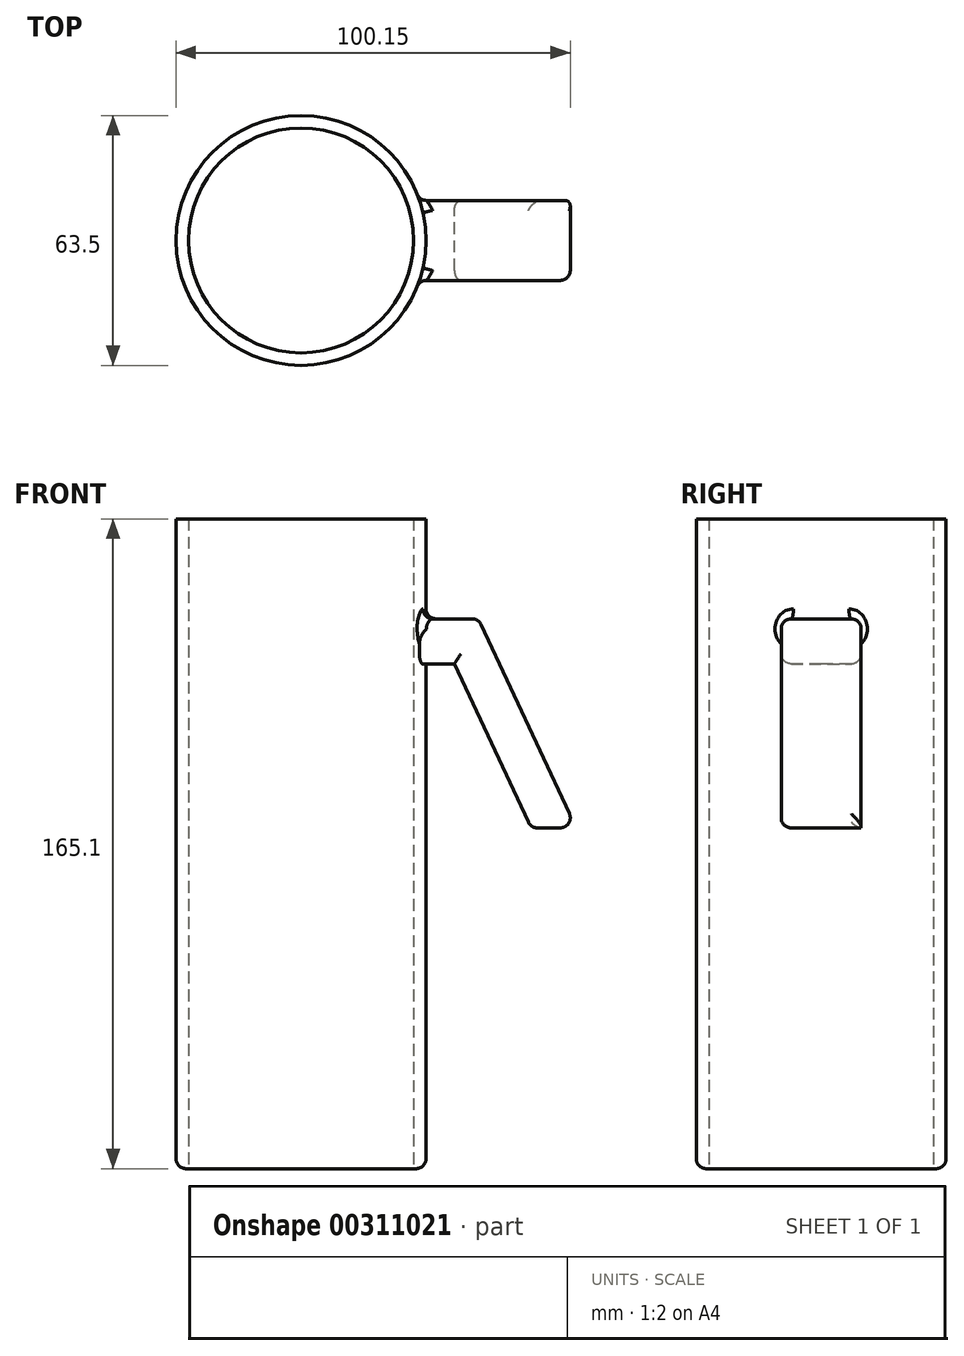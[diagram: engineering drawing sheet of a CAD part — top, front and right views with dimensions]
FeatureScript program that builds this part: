
annotation { "Feature Type Name" : "Feature", "Feature Type Description" : "" }
export const myFeature = defineFeature(function(context is Context, id is Id, definition is map)
    precondition{}
    {
        {
            var Q0;
            Q0=qCreatedBy(makeId("Front.planeOp"),FACE);
            var sketch = newSketch(context, id + "F0", { "sketchPlane" : qUnion([Q0])});
            skLineSegment(sketch, "E0.bottom", {"start": v(31.75, -82.55) * mm, "end": v(-31.75, -82.55) * mm});
            skLineSegment(sketch, "E0.top", {"start": v(31.75, 82.55) * mm, "end": v(-31.75, 82.55) * mm});
            skLineSegment(sketch, "E0.left", {"start": v(31.75, -82.55) * mm, "end": v(31.75, 82.55) * mm});
            skLineSegment(sketch, "E0.right", {"start": v(-31.75, -82.55) * mm, "end": v(-31.75, 82.55) * mm});
            skPoint(sketch, "E0.middle", {"position": v(0, 0) * mm});
            skLineSegment(sketch, "E1", {"start": v(-28.58, 82.55) * mm, "end": v(-28.57, -79.38) * mm});
            skLineSegment(sketch, "E2", {"start": v(-28.57, -79.38) * mm, "end": v(29.2, -79.38) * mm});
            skLineSegment(sketch, "E3", {"start": v(29.2, -79.38) * mm, "end": v(29.21, 82.55) * mm});
            skLineSegment(sketch, "E4", {"start": v(29.21, 57.15) * mm, "end": v(45.09, 57.15) * mm});
            skLineSegment(sketch, "E5", {"start": v(45.09, 57.15) * mm, "end": v(69.85, 4.04) * mm});
            skLineSegment(sketch, "E6", {"start": v(69.85, 4.04) * mm, "end": v(58.42, 4.04) * mm});
            skLineSegment(sketch, "E7", {"start": v(58.42, 4.04) * mm, "end": v(38.98, 45.72) * mm});
            skLineSegment(sketch, "E8", {"start": v(38.98, 45.72) * mm, "end": v(29.21, 45.72) * mm});
            skSolve(sketch);
        }
        {
            var Q0;
            Q0=qCreatedBy(makeId("Top.planeOp"),FACE);
            var sketch = newSketch(context, id + "F1", { "sketchPlane" : qUnion([Q0])});
            skCircle(sketch, "E9", {"center": v(0, 0) * mm, "radius": 28.58 * mm});
            skCircle(sketch, "E10", {"center": v(0, 0) * mm, "radius": 31.75 * mm});
            skSolve(sketch);
        }
        {
            var Q0;
            Q0=makeQuery(id+"F1.imprint","IMPRINT",FACE,{"disambiguationData":[TD([[makeQuery(id+"F1.imprint","IMPRINT",EDGE,{"derivedFrom":sQuery(id+"F1.wireOp",EDGE,"E9")}),-1.0]])]});
            extrude(context, id + "F2", {"entities" : qUnion([Q0]), "depth" : 82.55 * mm});
        }
        {
            var Q0;
            Q0=makeQuery(id+"F2.opExtrude","CAP_FACE",FACE,{"disambiguationData":[OSD([sQuery(id+"F1.wireOp",EDGE,"E9"),sQuery(id+"F1.wireOp",EDGE,"E10")])],"isStart":true});
            extrude(context, id + "F3", {"entities" : qUnion([Q0]), "operationType" : NewBodyOperationType.ADD, "depth" : 82.55 * mm});
        }
        {
            var Q0;
            {var subQ5=sQuery(id+"F0.wireOp",EDGE,"E5");Q0=makeQuery(id+"F0.imprint","IMPRINT",FACE,{"disambiguationData":[TD([[makeQuery(id+"F0.imprint","IMPRINT",EDGE,{"derivedFrom":subQ5}),-1.0]])]});}
            var Q1;
            {var subQ0=sQuery(id+"F0.wireOp",EDGE,"E8");var subQ1=sQuery(id+"F0.wireOp",EDGE,"E0.left");var subQ2=makeQuery(id+"F0.imprint","INTERSECT",VERTEX,{"derivedFrom":[subQ1,subQ0]});Q1=makeQuery(id+"F0.imprint","IMPRINT",FACE,{"disambiguationData":[TD([[makeQuery(id+"F0.imprint","IMPRINT",EDGE,{"disambiguationData":[TD([[subQ2,-1.0]])],"derivedFrom":subQ1}),1.0]])]});}
            extrude(context, id + "F4", {"entities" : qUnion([Q0, Q1]), "operationType" : NewBodyOperationType.ADD, "endBound" : BoundingType.SYMMETRIC, "depth" : 20.32 * mm});
        }
        {
            var Q0;
            Q0=makeQuery(id+"F4.opExtrude","CAP_EDGE",EDGE,{"disambiguationData":[OSD([sQuery(id+"F0.wireOp",EDGE,"E4")])],"isStart":true});
            var Q1;
            Q1=makeQuery(id+"F4.opExtrude","CAP_EDGE",EDGE,{"disambiguationData":[OSD([sQuery(id+"F0.wireOp",EDGE,"E0.left")])],"isStart":true});
            var Q2;
            Q2=makeQuery(id+"F4.opExtrude","CAP_EDGE",EDGE,{"disambiguationData":[OSD([sQuery(id+"F0.wireOp",EDGE,"E8")])],"isStart":true});
            var Q3;
            Q3=makeQuery(id+"F4.opExtrude","CAP_EDGE",EDGE,{"disambiguationData":[OSD([sQuery(id+"F0.wireOp",EDGE,"E7")])],"isStart":true});
            var Q4;
            Q4=makeQuery(id+"F4.opExtrude","CAP_EDGE",EDGE,{"disambiguationData":[OSD([sQuery(id+"F0.wireOp",EDGE,"E5")])],"isStart":true});
            var Q5;
            Q5=makeQuery(id+"F4.opExtrude","CAP_EDGE",EDGE,{"disambiguationData":[OSD([sQuery(id+"F0.wireOp",EDGE,"E5")])],"isStart":false});
            var Q6;
            Q6=makeQuery(id+"F4.opExtrude","SWEPT_EDGE",EDGE,{"disambiguationData":[OSD([sQuery(id+"F0.wireOp",EDGE,"E4"),sQuery(id+"F0.wireOp",EDGE,"E5")])]});
            var Q7;
            Q7=makeQuery(id+"F4.opExtrude","SWEPT_FACE",FACE,{"disambiguationData":[OSD([sQuery(id+"F0.wireOp",EDGE,"E4")])]});
            var Q8;
            Q8=makeQuery(id+"F4.opExtrude","SWEPT_EDGE",EDGE,{"disambiguationData":[OSD([sQuery(id+"F0.wireOp",EDGE,"E5"),sQuery(id+"F0.wireOp",EDGE,"E6")])]});
            var Q9;
            Q9=makeQuery(id+"F4.opExtrude","CAP_EDGE",EDGE,{"disambiguationData":[OSD([sQuery(id+"F0.wireOp",EDGE,"E6")])],"isStart":false});
            var Q10;
            Q10=makeQuery(id+"F4.opExtrude","SWEPT_EDGE",EDGE,{"disambiguationData":[OSD([sQuery(id+"F0.wireOp",EDGE,"E6"),sQuery(id+"F0.wireOp",EDGE,"E7")])]});
            var Q11;
            Q11=makeQuery(id+"F4.opExtrude","CAP_EDGE",EDGE,{"disambiguationData":[OSD([sQuery(id+"F0.wireOp",EDGE,"E7")])],"isStart":false});
            var Q12;
            Q12=makeQuery(id+"F4.opExtrude","CAP_EDGE",EDGE,{"disambiguationData":[OSD([sQuery(id+"F0.wireOp",EDGE,"E8")])],"isStart":false});
            var Q13;
            Q13=makeQuery(id+"F3.opExtrude","CAP_EDGE",EDGE,{"disambiguationData":[OSD([sQuery(id+"F1.wireOp",EDGE,"E10")])],"isStart":false});
            fillet(context, id + "F5", {"entities" : qUnion([Q0, Q1, Q2, Q3, Q4, Q5, Q6, Q7, Q8, Q9, Q10, Q11, Q12, Q13]), "radius" : 2.54 * mm, "tangentPropagation" : true, "allowEdgeOverflow" : false});
        }
    });
